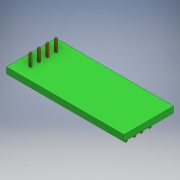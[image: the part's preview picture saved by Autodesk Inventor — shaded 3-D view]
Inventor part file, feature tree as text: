
AUTODESK INVENTOR PART (.ipt)
format: ipt  version: 2018.3 (Build 223284000, 284)  size: 250,368 bytes
history: native  units: mm
features: chamfer x16, extrude x8, sketch x8
ambient origin geometry x8: Origin, YZ Plane, XZ Plane, XY Plane, X Axis, Y Axis, Z Axis, Center Point
bodies: Solid1 (feature_tree)
feature tree (32):
  extrude  "Extrusion1"  Depth=13.7mm
  extrude  "Extrusion2"  Depth=6.0mm
  extrude  "Extrusion3"  Depth=0.5mm TaperAngle=0.0deg
  chamfer  "Chamfer1"  Distance=3.5mm
  chamfer  "Chamfer2"  Distance=0.5mm Angle=45.0deg
  extrude  "Extrusion4"  Depth=1.94mm
  chamfer  "Chamfer3"  Distance=3.5mm
  chamfer  "Chamfer4"  Distance=0.5mm Angle=45.0deg
  extrude  "Extrusion5"  Depth=1.94mm
  chamfer  "Chamfer5"  Distance=3.5mm
  chamfer  "Chamfer6"  Distance=0.5mm Angle=45.0deg
  chamfer  "Chamfer7"  Distance=0.5mm Angle=45.0deg
  chamfer  "Chamfer8"  Distance=0.5mm Angle=45.0deg
  sketch  "Sketch1"  dims[d0=32.5mm d1=13.7mm]
  sketch  "Sketch2"  dims[d2=1.7mm d3=0.0mm d4=6.0mm]
  sketch  "Sketch3"  dims[d5=6.0mm d6=0.5mm d7=0.0mm]
  sketch  "Sketch4"  dims[d8=0.6mm]
  sketch  "Sketch5"  dims[d9=0.4mm d10=3.5mm d11=0.0mm d12=0.15mm d13=0.5mm d14=45.0deg]
  sketch  "Sketch6"  dims[d15=0.15mm d16=0.5mm d17=45.0deg d19=1.94mm d20=3.5mm d21=0.0mm d22=0.15mm d23=0.5mm d24=45.0deg]
  sketch  "Sketch7"  dims[d25=0.15mm d26=0.5mm d27=45.0deg d28=1.94mm]
  sketch  "Sketch8"  dims[d29=1.94mm d30=3.5mm d31=0.0mm d32=0.15mm d33=0.5mm d34=45.0deg d35=0.15mm d36=0.5mm d37=45.0deg d38=0.15mm d39=0.5mm d40=45.0deg d41=0.15mm d42=0.5mm d43=45.0deg d44=3.0mm d45=3.14mm d49=3.0mm d50=3.14mm d51=0.6mm d52=0.4mm d54=0.0mm d55=3.5mm d56=45.0deg d57=0.5mm d58=0.15mm d59=45.0deg d60=0.5mm d61=0.15mm d64=0.0mm d65=3.5mm d66=45.0deg d67=0.5mm d68=0.15mm d69=45.0deg d70=0.5mm d71=0.15mm d75=0.0mm d76=3.5mm d77=45.0deg d78=0.5mm d79=0.15mm d80=45.0deg d81=0.5mm d82=0.15mm d83=45.0deg d84=0.5mm d85=0.15mm d86=45.0deg d87=0.5mm d88=0.15mm d89=1.94mm d90=0.4mm d91=0.6mm d92=1.94mm d93=1.94mm d94=0.4mm d95=0.6mm]
  extrude  "Extrusion6"  Depth=0.5mm TaperAngle=45.0deg
  extrude  "Extrusion7"  Depth=3.0mm
  extrude  "Extrusion8"  Depth=3.14mm
  chamfer  "Chamfer9"  Distance=0.5mm Angle=45.0deg
  chamfer  "Chamfer10"  Distance=0.5mm Angle=45.0deg
  chamfer  "Chamfer11"  Distance=3.5mm
  chamfer  "Chamfer12"  Distance=0.5mm Angle=45.0deg
  chamfer  "Chamfer13"  Distance=0.5mm Angle=45.0deg
  chamfer  "Chamfer14"  Distance=3.5mm
  chamfer  "Chamfer15"  Distance=0.5mm Angle=45.0deg
  chamfer  "Chamfer16"  Distance=0.5mm Angle=45.0deg
